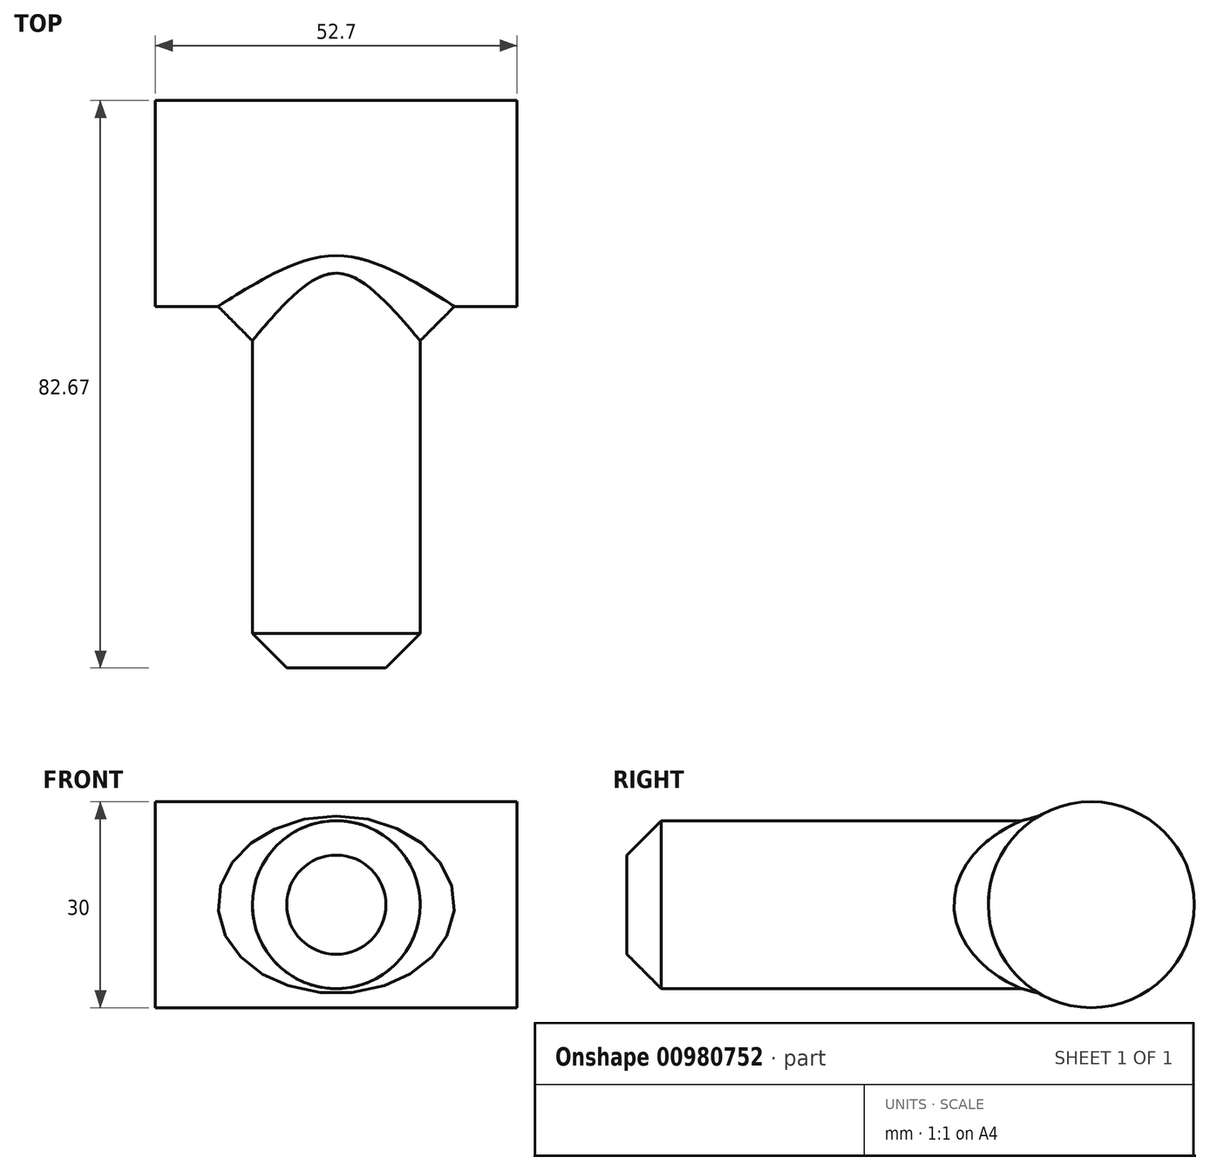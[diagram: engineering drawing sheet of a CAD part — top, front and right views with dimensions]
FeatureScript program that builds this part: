
annotation { "Feature Type Name" : "Feature", "Feature Type Description" : "" }
export const myFeature = defineFeature(function(context is Context, id is Id, definition is map)
    precondition{}
    {
        {
            var Q0;
            Q0=qCreatedBy(makeId("Right.planeOp"),FACE);
            var sketch = newSketch(context, id + "F0", { "sketchPlane" : qUnion([Q0])});
            skCircle(sketch, "E0", {"center": v(0, 0) * mm, "radius": 15 * mm});
            skSolve(sketch);
        }
        {
            var Q0;
            Q0=makeQuery(id+"F0.imprint","IMPRINT",FACE,{"disambiguationData":[TD([[makeQuery(id+"F0.imprint","IMPRINT",EDGE,{"derivedFrom":sQuery(id+"F0.wireOp",EDGE,"E0")}),1.0]])]});
            var Q1;
            Q1=sQuery(id+"F0.wireOp",EDGE,"E0");
            extrude(context, id + "F1", {"entities" : qUnion([Q0]), "surfaceEntities" : qUnion([Q1]), "depth" : 52.7 * mm, "offsetDistance" : 25 * mm, "symmetric" : true});
        }
        {
            var Q0;
            Q0=qCreatedBy(makeId("Front.planeOp"),FACE);
            var sketch = newSketch(context, id + "F2", { "sketchPlane" : qUnion([Q0])});
            skCircle(sketch, "E1", {"center": v(0, 0) * mm, "radius": 12.23 * mm});
            skSolve(sketch);
        }
        {
            var Q0;
            Q0 = qSketchRegion(id + "F2", true);
            var Q1;
            Q1=makeQuery(id+"F1.opExtrude","SWEPT_FACE",FACE,{"disambiguationData":[OSD([sQuery(id+"F0.wireOp",EDGE,"E0")])]});
            extrude(context, id + "F3", {"entities" : qUnion([Q0]), "operationType" : NewBodyOperationType.ADD, "endBound" : BoundingType.THROUGH_ALL, "depth" : 25 * mm, "endBoundEntityFace" : qUnion([Q1]), "hasOffset" : true, "offsetDistance" : 3 * mm, "offsetOppositeDirection" : true});
        }
        {
            var Q0;
            Q0=makeQuery(id+"F3.opExtrude","CAP_EDGE",EDGE,{"disambiguationData":[OSD([sQuery(id+"F2.wireOp",EDGE,"E1")])],"isStart":false});
            var Q1;
            Q1=makeQuery(id+"F3.boolean.opBoolean","INTERSECT",EDGE,{"derivedFrom":[makeQuery(id+"F1.opExtrude","SWEPT_FACE",FACE,{"disambiguationData":[OSD([sQuery(id+"F0.wireOp",EDGE,"E0")])]}),makeQuery(id+"F3.opExtrude","SWEPT_FACE",FACE,{"disambiguationData":[OSD([sQuery(id+"F2.wireOp",EDGE,"E1")])]})]});
            chamfer(context, id + "F4", {"entities" : qUnion([Q0, Q1]), "width" : 5 * mm, "tangentPropagation" : true});
        }
    });
